# Revit family: Safety-Railing_Section_SafetyRail_Accu-Fit-Mounted-Architectural
name_source: partatom
category: Railings
units: mm (PartAtom-declared; Revit-internal decimal feet)

## family parameters
Classification Number = 23.30.80.11
Cut with Voids When Loaded = No
Shared = No

## types (4) — shared parameters
Construction Details = http://www.arcat.com
Green Building-LEED = http://www.arcat.com
Keynote = 05 52 00
Manufacturer = Safety Rail Company
Manufacturer Fax = 888-471-4931
Manufacturer Website = http://www.safetyrailcompany.com
Post OD = 0' - 1 5/8"
Product Data = http://www.arcat.com
Product Properties = http://www.safetyrailcompany.com
Revision = R1_2017-08
Sales Information = http://www.safetyrailcompany.com
SpecWizard = http://www.arcat.com
Specification = http://www.arcat.com
Standards Conformance = OSHA Guardrail Reg 1910.23, 1926.500 - .503  ;  Made in USA
URL = http://www.safetyrailcompany.com
Unit Height = 3' - 6"
zero-valued in all types: Expected Lifespan (Years), Maintenance Schedule (Months), Warranty Duration (Years)

## per-type parameters (varying)
| type | Base Type | Base Weight | Description | Model |
| Corrugated | Base_SafetyRail_MetalRoof : Corrugated Mount - Single | as Specified | Safety Rail Company Fall Protection System - Accu-Fit Architectural for Corrugated Roof as Specified | Accu-Fit Architectural Mounted Corrugated |
| R Panel | Base_SafetyRail_MetalRoof : R Panel Mount - Single | as Specified | Safety Rail Company Fall Protection System - Accu-Fit Architectural for R Panel Roof as Specified | Accu-Fit Architectural Mounted R Panel |
| Standing Seam 24 inch Spacing | Base_SafetyRail_MetalRoof : Standing Seam Clamp - 24 | 26 lbs per Base | Safety Rail Company Fall Protection System - Accu-Fit Architectural for Standing Seam Roof as Specified | Accu-Fit Architectural Mounted Standing Seam |
| Standing Seam 16 to 18 inch Spacing | Base_SafetyRail_MetalRoof : Standing Seam Clamp 16-18 | as Specified | Safety Rail Company Fall Protection System - Accu-Fit Architectural for Standing Seam Roof as Specified | Accu-Fit Architectural Mounted Standing Seam |

## geometry (parser evidence)
native form markers: Sweep x10
no freeform markers — native parametric forms only
